# Revit family: TallUnit-45cm-SingleCover-Left-Vitra-NestTrendySeries-56427+56186+56187+56188
name_source: partatom
category: Furniture
revit_build: Autodesk Revit 2017 (Build: 20160225_1515(x64)
units: mm (PartAtom-declared; Revit-internal decimal feet)

## family parameters
Cut with Voids When Loaded = No
Host = Face
OmniClass Number = 23.40.20.00
OmniClass Title = General Furniture and Specialties
Room Calculation Point = No
Shared = Yes

## types (4) — shared parameters
BIMobject category = Storage
Brand = VitrA
Default Elevation = 660 mm
Description = Nest Trendy Tall Unit
Design country = Turkey
IFC Classification = Furniture
Main Material = Wood
Manufacturer = Vitra
Manufacturer name = VitrA
Masterformat 2014 Code = 12 35 30.23
Masterformat 2014 Description = Bathroom Casework
Mounting type = Wall-Hung
NBS Referans Code = 35-75-08
NBS Referans Description = Bathroom Cabinets
Nominal Depth (mm) = 370 mm
Nominal Height (mm) = 1600 mm  [stored 5.24934 ft]
Nominal Width (mm) = 460 mm  [stored 1.50919 ft]
OmniClass Code = 23-31 25 13
OmniClass Description = Bathroom Cabinets
Product certification = https://www.vitraglobal.com
Product family = Nest Trendy
Product group = Bathroom Furniture
Product url = https://www.vitraglobal.com
Secondary Material = Metal
Technical description = https://www.vitraglobal.com
UNSPSC Code = 30161801
UNSPSC Description = Bathroom Cabinets
URL = https://vitraglobal.com
Uniclass 1.4 Code = L8241
Uniclass 1.4 Description = Bathroom Cabinets
Uniclass 2.0 Code = PR-35-75-08
Uniclass 2.0 Description = Bathroom Cabinets
Uniclass 2015 Code = Pr_40_30_78_03
Uniclass 2015 Name = Bathroom Cabinets
Uniformat II Code = E2010
Uniformat II Description = Fixed Furnishings
Warranty Period (Year) = 2
Youtube = https://www.youtube.com

## per-type parameters (varying)
| type | Article No. (default) | Color | Model | Primary Material | Product SKU | Product data url |
| TallUnit-45cm-SingleCover-Left-Vitra-NestTrendySeries-56427 | 56427 | High Gloss White | 56427 | High Gloss White | 56427 | https://www.bimobject.com |
| TallUnit-45cm-SingleCover-Left-Vitra-NestTrendySeries-56186 | 56186 | High Gloss Anthracite | 56186 | High Gloss Anthracite | 56186 |  |
| TallUnit-45cm-SingleCover-Left-Vitra-NestTrendySeries-56187 | 56187 | Waved Natural Wood | 56187 | Waved Natural Wood | 56187 |  |
| TallUnit-45cm-SingleCover-Left-Vitra-NestTrendySeries-56188 | 56188 | Grey Natural Wood | 56188 | Grey Natural Wood | 56188 |  |

note: [stored X ft] marks values corroborated as IEEE doubles in the binary element streams (Revit-internal decimal feet)

## geometry (parser evidence)
native form markers: Sweep x2
no freeform markers — native parametric forms only
